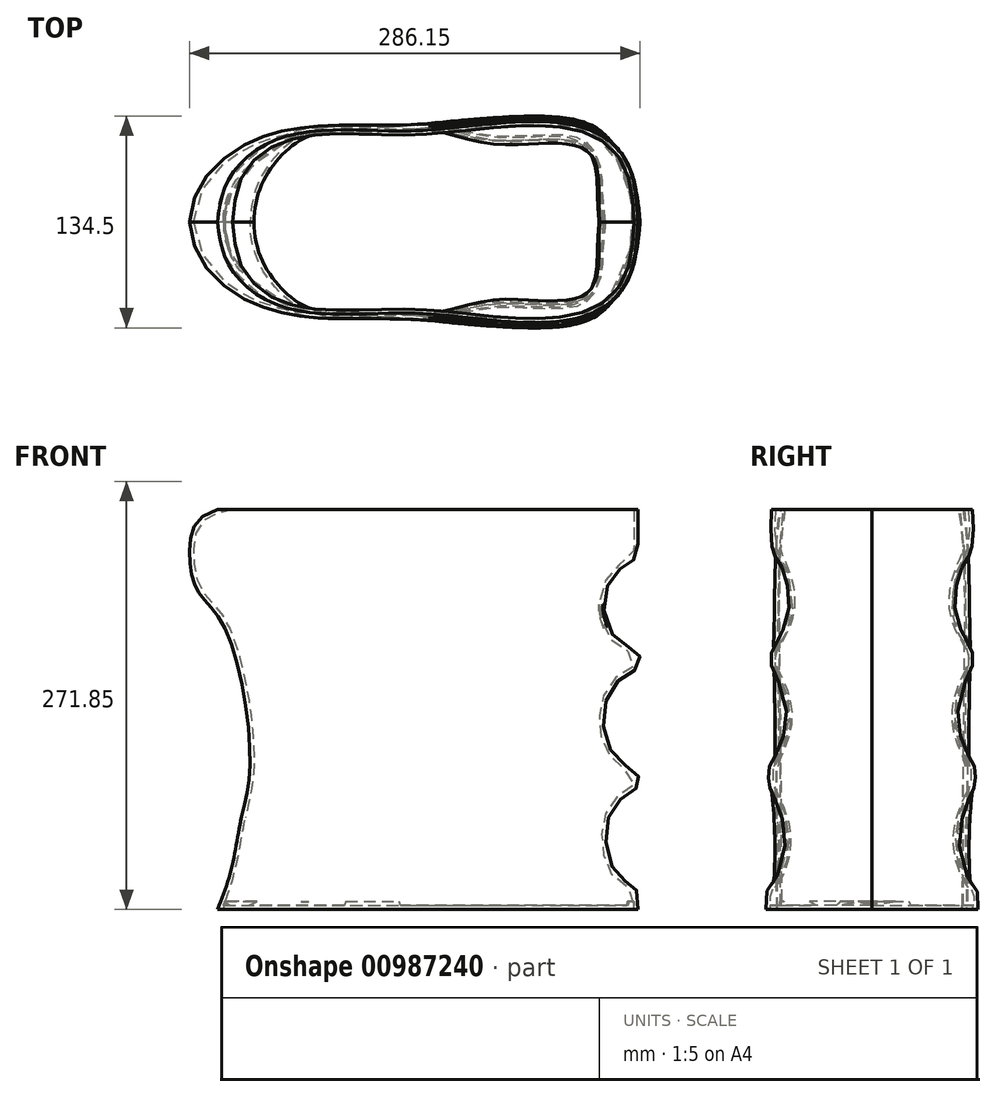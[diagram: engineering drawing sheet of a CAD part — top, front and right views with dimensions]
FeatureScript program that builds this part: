
annotation { "Feature Type Name" : "Feature", "Feature Type Description" : "" }
export const myFeature = defineFeature(function(context is Context, id is Id, definition is map)
    precondition{}
    {
        {
            var Q0;
            Q0=qCreatedBy(makeId("Right.planeOp"),FACE);
            cPlane(context, id + "F0", {"entities" : qUnion([Q0]), "cplaneType" : CPlaneType.OFFSET, "offset" : 66.04 * mm, "width" : 152.4 * mm, "height" : 152.4 * mm});
        }
        {
            var Q0;
            Q0=qCreatedBy(makeId("Top.planeOp"),FACE);
            var sketch = newSketch(context, id + "F1", { "sketchPlane" : qUnion([Q0])});
            skLineSegment(sketch, "E0", {"start": v(-122.98, 0) * mm, "end": v(144.02, 0) * mm});
            skFitSpline(sketch, "E1", {"points": [v(-122.98, 0) * mm, v(-115.91, 27) * mm, v(-86.53, 52) * mm, v(-38.29, 58.58) * mm, v(6.89, 58.14) * mm, v(77.06, 63.85) * mm, v(120.48, 55.07) * mm, v(138.9, 33.58) * mm, v(144.02, 0) * mm], "startDerivative": vector(33.33, 267.65) * mm, "endDerivative": vector(16.88, -313.23) * mm});
            skPoint(sketch, "E2", {"position": v(0, 57.87) * mm});
            skPoint(sketch, "E3", {"position": v(66.04, 63.48) * mm});
            skSolve(sketch);
        }
        {
            var Q0;
            Q0=qCreatedBy(makeId("Top.planeOp"),FACE);
            cPlane(context, id + "F2", {"entities" : qUnion([Q0]), "cplaneType" : CPlaneType.OFFSET, "offset" : 254 * mm, "oppositeDirection" : true, "width" : 152.4 * mm, "height" : 152.4 * mm});
        }
        {
            var Q0;
            Q0=qCreatedBy(id+"F2.planeOp",FACE);
            var sketch = newSketch(context, id + "F3", { "sketchPlane" : qUnion([Q0])});
            skLineSegment(sketch, "E4", {"start": v(-122.98, 0) * mm, "end": v(144.02, 0) * mm});
            skFitSpline(sketch, "E5", {"points": [v(-122.98, 0) * mm, v(-105.3, 37.86) * mm, v(-71.04, 58.4) * mm, v(-32.36, 59.93) * mm, v(6.04, 62.08) * mm, v(76.48, 67.24) * mm, v(118.67, 59) * mm, v(135.73, 35.74) * mm, v(144.02, 0) * mm], "startDerivative": vector(-8.7, 417.24) * mm, "endDerivative": vector(63.83, -452.37) * mm});
            skPoint(sketch, "E6", {"position": v(0, 61.5) * mm});
            skPoint(sketch, "E7", {"position": v(66.04, 66.98) * mm});
            skSolve(sketch);
        }
        {
            var Q0;
            Q0=qCreatedBy(makeId("Front.planeOp"),FACE);
            var sketch = newSketch(context, id + "F4", { "sketchPlane" : qUnion([Q0])});
            skFitSpline(sketch, "E8", {"points": [v(144.02, -254) * mm, v(141.96, -239.75) * mm, v(131.38, -232.53) * mm, v(123.57, -207.45) * mm, v(131.61, -185.2) * mm, v(144.02, -175.98) * mm, v(144.02, -168.87) * mm, v(131.58, -158.87) * mm, v(122, -135.65) * mm, v(130.45, -109.9) * mm, v(144.02, -100.2) * mm, v(144.02, -91) * mm, v(131.82, -83.9) * mm, v(122.28, -58.47) * mm, v(132.32, -38.22) * mm, v(141.98, -31.29) * mm, v(144.02, 0) * mm], "startDerivative": vector(36.7, 365.1) * mm, "endDerivative": vector(0, 683.5) * mm});
            skFitSpline(sketch, "E9", {"points": [v(-122.98, 0) * mm, v(-140.58, -29.01) * mm, v(-134.9, -52.68) * mm, v(-118.8, -73.97) * mm, v(-102.24, -159.64) * mm, v(-108.12, -197.5) * mm, v(-122.98, -254) * mm], "startDerivative": vector(-340.66, -92.34) * mm, "endDerivative": vector(-151.86, -332.93) * mm});
            skPoint(sketch, "E10", {"position": v(-109.02, -103.43) * mm});
            skPoint(sketch, "E11", {"position": v(-103.6, -135.72) * mm});
            skLineSegment(sketch, "E12", {"start": v(144.02, -254) * mm, "end": v(144.02, 0) * mm});
            skSolve(sketch);
        }
        {
            var Q0;
            Q0=qCreatedBy(makeId("Right.planeOp"),FACE);
            var sketch = newSketch(context, id + "F5", { "sketchPlane" : qUnion([Q0])});
            skFitSpline(sketch, "E13", {"points": [v(57.87, 0) * mm, v(61.5, -39.68) * mm, v(61.5, -142.46) * mm, v(61.5, -216.72) * mm, v(61.5, -254) * mm], "startDerivative": vector(31.11, -200.55) * mm, "endDerivative": vector(-2.97, -268.86) * mm});
            skSolve(sketch);
        }
        {
            var Q0;
            Q0=qCreatedBy(id+"F0.planeOp",FACE);
            var sketch = newSketch(context, id + "F6", { "sketchPlane" : qUnion([Q0])});
            skFitSpline(sketch, "E14", {"points": [v(63.48, 0) * mm, v(63.16, -23.52) * mm, v(61.29, -28.9) * mm, v(58.2, -33.26) * mm, v(51.72, -60.7) * mm, v(60.74, -84.97) * mm, v(63.32, -89.95) * mm, v(63.12, -100.44) * mm, v(60.61, -105.8) * mm, v(53.42, -132.07) * mm, v(62.62, -159.35) * mm, v(65.3, -164.37) * mm, v(64.96, -174.4) * mm, v(62.62, -180.6) * mm, v(54.42, -207.54) * mm, v(61.56, -235.94) * mm, v(66.13, -241.37) * mm, v(66.98, -254) * mm], "startDerivative": vector(27.94, -350.47) * mm, "endDerivative": vector(16.86, -447.43) * mm});
            skSolve(sketch);
        }
        {
            var Q0;
            Q0=makeQuery(id+"F1.imprint","IMPRINT",FACE,{"disambiguationData":[TD([[makeQuery(id+"F1.imprint","IMPRINT",EDGE,{"derivedFrom":sQuery(id+"F1.wireOp",EDGE,"E0")}),1.0]])]});
            var Q1;
            Q1=makeQuery(id+"F3.imprint","IMPRINT",FACE,{"disambiguationData":[TD([[makeQuery(id+"F3.imprint","IMPRINT",EDGE,{"derivedFrom":sQuery(id+"F3.wireOp",EDGE,"E4")}),1.0]])]});
            var Q2;
            Q2=sQuery(id+"F4.wireOp",EDGE,"E8");
            var Q3;
            Q3=sQuery(id+"F6.wireOp",EDGE,"E14");
            var Q4;
            Q4=sQuery(id+"F5.wireOp",EDGE,"E13");
            var Q5;
            Q5=sQuery(id+"F4.wireOp",EDGE,"E9");
            loft(context, id + "F7", {"addGuides" : true, "sheetProfilesArray" : [{ "sheetProfileEntities" : qUnion([Q0]) }, { "sheetProfileEntities" : qUnion([Q1]) }], "guidesArray" : [{ "guideEntities" : qUnion([Q2]), "guideDerivativeType" : LoftGuideDerivativeType.DEFAULT, "guideDerivativeMagnitude" : 1 }, { "guideEntities" : qUnion([Q3]), "guideDerivativeType" : LoftGuideDerivativeType.DEFAULT, "guideDerivativeMagnitude" : 1 }, { "guideEntities" : qUnion([Q4]), "guideDerivativeType" : LoftGuideDerivativeType.DEFAULT, "guideDerivativeMagnitude" : 1 }, { "guideEntities" : qUnion([Q5]), "guideDerivativeType" : LoftGuideDerivativeType.DEFAULT, "guideDerivativeMagnitude" : 1 }]});
        }
        {
            var Q0;
            Q0=makeQuery(id+"F7.opLoft","SWEPT_BODY",BODY,{"disambiguationData":[OSD([makeQuery(id+"F1.imprint","IMPRINT",FACE,{"disambiguationData":[TD([[makeQuery(id+"F1.imprint","IMPRINT",EDGE,{"derivedFrom":sQuery(id+"F1.wireOp",EDGE,"E0")}),1.0]])]}),makeQuery(id+"F3.imprint","IMPRINT",FACE,{"disambiguationData":[TD([[makeQuery(id+"F3.imprint","IMPRINT",EDGE,{"derivedFrom":sQuery(id+"F3.wireOp",EDGE,"E4")}),1.0]])]}),sQuery(id+"F4.wireOp",EDGE,"E8"),sQuery(id+"F4.wireOp",EDGE,"E9"),sQuery(id+"F5.wireOp",EDGE,"E13"),sQuery(id+"F6.wireOp",EDGE,"E14")])]});
            var Q1;
            Q1=qCreatedBy(makeId("Front.planeOp"),FACE);
            mirror(context, id + "F8", {"operationType" : NewBodyOperationType.ADD, "entities" : qUnion([Q0]), "mirrorPlane" : qUnion([Q1])});
        }
        {
            var Q0;
            {var subQ0=makeQuery(id+"F7.opLoft","CAP_FACE",FACE,{"disambiguationData":[OSD([makeQuery(id+"F1.imprint","IMPRINT",FACE,{"disambiguationData":[TD([[makeQuery(id+"F1.imprint","IMPRINT",EDGE,{"derivedFrom":sQuery(id+"F1.wireOp",EDGE,"E0")}),1.0]])]})])],"isStart":true});Q0=makeQuery(id+"F8.boolean.opBoolean","MERGE",FACE,{"derivedFrom":[subQ0,makeQuery(id+"F8.opPattern","COPY",FACE,{"derivedFrom":subQ0,"instanceName":"1"})]});}
            shell(context, id + "F9", {"entities" : qUnion([Q0]), "thickness" : 2.5 * mm});
        }
        {
            var Q0;
            {var subQ0=makeQuery(id+"F7.opLoft","CAP_FACE",FACE,{"disambiguationData":[OSD([makeQuery(id+"F3.imprint","IMPRINT",FACE,{"disambiguationData":[TD([[makeQuery(id+"F3.imprint","IMPRINT",EDGE,{"derivedFrom":sQuery(id+"F3.wireOp",EDGE,"E4")}),1.0]])]})])],"isStart":true});Q0=makeQuery(id+"F8.boolean.opBoolean","MERGE",FACE,{"derivedFrom":[subQ0,makeQuery(id+"F8.opPattern","COPY",FACE,{"derivedFrom":subQ0,"instanceName":"1"})]});}
            var sketch = newSketch(context, id + "F10", { "sketchPlane" : qUnion([Q0])});
            skFitSpline(sketch, "E15", {"points": [v(-118.78, 0) * mm, v(-114.94, -17.2) * mm, v(-99.8, -36.7) * mm, v(-71.57, -54.66) * mm, v(-37.7, -57.22) * mm, v(0, -58.5) * mm, v(66.49, -63.9) * mm, v(116.01, -56.97) * mm, v(133.98, -32.33) * mm, v(141.67, 0.58) * mm, v(125.77, 47.99) * mm, v(102.16, 62.62) * mm, v(50.58, 63.39) * mm, v(0, 58.77) * mm, v(-50.78, 57.74) * mm, v(-74.65, 54.15) * mm, v(-101.6, 36.7) * mm, v(-113.14, 24.12) * mm, v(-118.78, 0) * mm]});
            skSolve(sketch);
        }
        {
            var Q0;
            Q0 = qSketchRegion(id + "F10", true);
            extrude(context, id + "F11", {"entities" : qUnion([Q0]), "operationType" : NewBodyOperationType.REMOVE, "oppositeDirection" : true, "depth" : 5 * mm, "offsetDistance" : 25 * mm});
        }
    });
